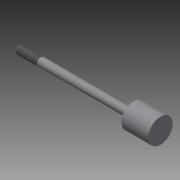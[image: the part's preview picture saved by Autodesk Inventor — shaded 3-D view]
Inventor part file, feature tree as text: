
AUTODESK INVENTOR PART (.ipt)
format: ipt  version: 2014 SP2 (Build 180246200, 246)  size: 139,776 bytes
history: native  units: in
note: dims shown in document units (in); Inventor stores cm internally (conversion verified against a paired STEP export)
features: other x70, revolve x3, sketch x3, thread x1
ambient origin geometry x8: Origin, YZ Plane, XZ Plane, XY Plane, X Axis, Y Axis, Z Axis, Center Point
bodies: Solid1 (feature_tree)
feature tree (77):
  revolve  "Revolution1"  Angle=360.0deg
  revolve  "Revolution2"  Angle=360.0deg
  thread  "Thread1"  [1 undecoded]
  revolve  "Revolution3"  [1 undecoded]
  other  "dia1_XY"
  other  "dia1_YZ"
  other  "dia1_ZX"
  other  "dia1_X"
  other  "dia1_Y"
  other  "dia1_Z"
  other  "dia1_Center"
  other  "dia12_XY"
  other  "dia12_YZ"
  other  "dia12_ZX"
  other  "dia12_X"
  other  "dia12_Y"
  other  "dia12_Z"
  other  "dia12_Center"
  other  "dia2_XY"
  other  "dia2_YZ"
  other  "dia2_ZX"
  other  "dia2_X"
  other  "dia2_Y"
  other  "dia2_Z"
  other  "dia2_Center"
  other  "dia22_XY"
  other  "dia22_YZ"
  other  "dia22_ZX"
  other  "dia22_X"
  other  "dia22_Y"
  other  "dia22_Z"
  other  "dia22_Center"
  other  "rl1_XY"
  other  "rl1_YZ"
  other  "rl1_ZX"
  other  "rl1_X"
  other  "rl1_Y"
  other  "rl1_Z"
  other  "rl1_Center"
  other  "rl2_XY"
  other  "rl2_YZ"
  other  "rl2_ZX"
  other  "rl2_X"
  other  "rl2_Y"
  other  "rl2_Z"
  other  "rl2_Center"
  other  "rod_cp_XY"
  other  "rod_cp_YZ"
  other  "rod_cp_ZX"
  other  "rod_cp_X"
  other  "rod_cp_Y"
  other  "rod_cp_Z"
  other  "rod_cp_Center"
  other  "thd1_XY"
  other  "thd1_YZ"
  other  "thd1_ZX"
  other  "thd1_X"
  other  "thd1_Y"
  other  "thd1_Z"
  other  "thd1_Center"
  other  "thd2_XY"
  other  "thd2_YZ"
  other  "thd2_ZX"
  other  "thd2_X"
  other  "thd2_Y"
  other  "thd2_Z"
  other  "thd2_Center"
  other  "to_rod_clevis_XY"
  other  "to_rod_clevis_YZ"
  other  "to_rod_clevis_ZX"
  other  "to_rod_clevis_X"
  other  "to_rod_clevis_Y"
  other  "to_rod_clevis_Z"
  other  "to_rod_clevis_Center"
  sketch  "Sketch_1"  dims[d0=360.0deg d1=360.0deg]
  sketch  "Sketch_3"  dims[d2=0.4814in d3=0.0in d4=360.0deg]
  sketch  "Sketch_30"  dims[d5=0.0in d6=0.0in d7=0.0in d8=0.0in d9=0.0in d10=0.0in]
note: 2 required parameter values undecoded (feature->parameter linkage not recoverable at this tier; creation-order binding heuristic only, values carry confidence <= 0.55)
